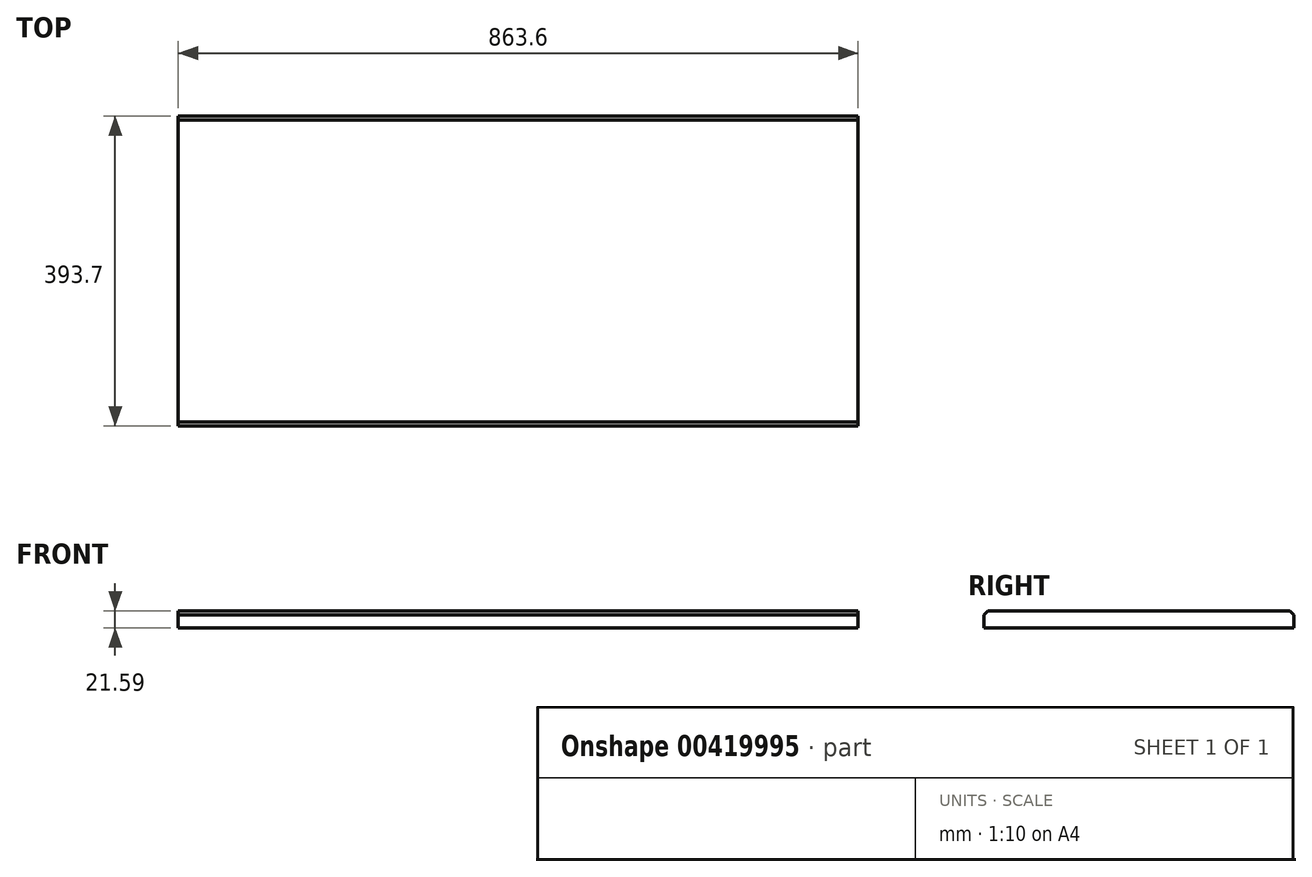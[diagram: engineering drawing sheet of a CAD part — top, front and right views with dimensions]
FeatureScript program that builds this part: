
annotation { "Feature Type Name" : "Feature", "Feature Type Description" : "" }
export const myFeature = defineFeature(function(context is Context, id is Id, definition is map)
    precondition{}
    {
        {
            var Q0;
            Q0=qCreatedBy(makeId("Front.planeOp"),FACE);
            var sketch = newSketch(context, id + "F0", { "sketchPlane" : qUnion([Q0])});
            skLineSegment(sketch, "E0.bottom", {"start": v(-410, -11.43) * mm, "end": v(453.6, -11.43) * mm});
            skLineSegment(sketch, "E0.top", {"start": v(-410, -33.02) * mm, "end": v(453.6, -33.02) * mm});
            skLineSegment(sketch, "E1", {"start": v(-410, -11.43) * mm, "end": v(-410, -33.02) * mm});
            skLineSegment(sketch, "E2", {"start": v(453.6, -11.43) * mm, "end": v(453.6, -33.02) * mm});
            skPoint(sketch, "E3.end.orphan", {"position": v(-457.16, 0) * mm});
            skSolve(sketch);
        }
        {
            var Q0;
            Q0=makeQuery(id+"F0.imprint","IMPRINT",FACE,{"disambiguationData":[TD([[makeQuery(id+"F0.imprint","IMPRINT",EDGE,{"derivedFrom":sQuery(id+"F0.wireOp",EDGE,"E0.bottom")}),-1.0]])]});
            extrude(context, id + "F1", {"entities" : qUnion([Q0]), "depth" : 393.7 * mm});
        }
        {
            var Q0;
            Q0=makeQuery(id+"F1.opExtrude","CAP_EDGE",EDGE,{"disambiguationData":[OSD([sQuery(id+"F0.wireOp",EDGE,"E0.bottom")])],"isStart":false});
            var Q1;
            Q1=makeQuery(id+"F1.opExtrude","CAP_EDGE",EDGE,{"disambiguationData":[OSD([sQuery(id+"F0.wireOp",EDGE,"E0.bottom")])],"isStart":true});
            chamfer(context, id + "F2", {"entities" : qUnion([Q0, Q1]), "width" : 5.08 * mm, "tangentPropagation" : true});
        }
    });
